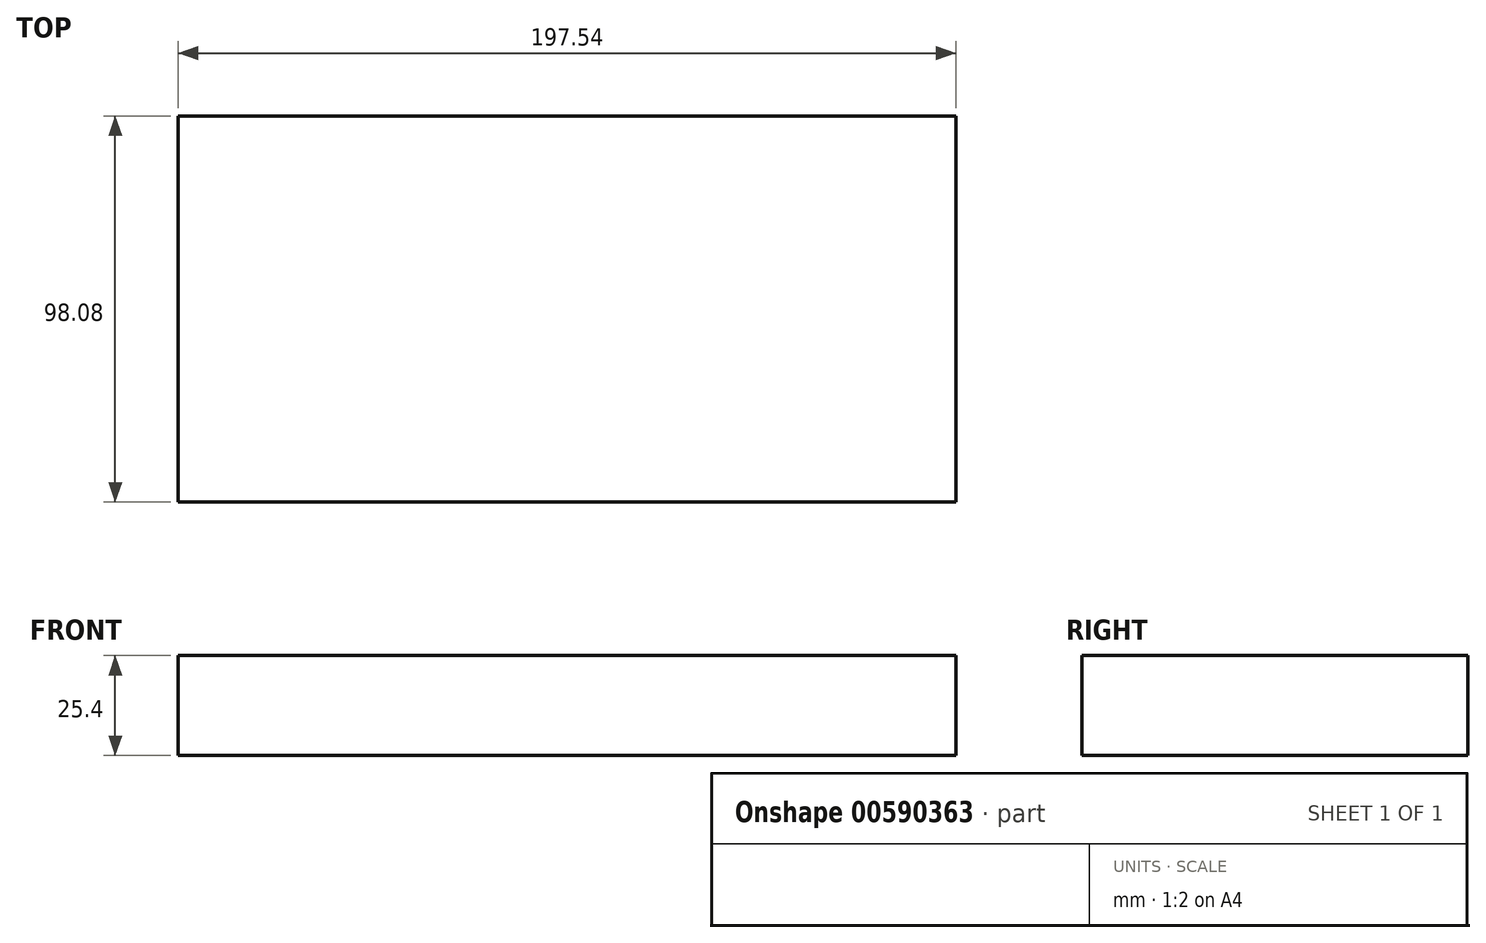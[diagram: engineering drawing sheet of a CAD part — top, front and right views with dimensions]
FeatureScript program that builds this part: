
annotation { "Feature Type Name" : "Feature", "Feature Type Description" : "" }
export const myFeature = defineFeature(function(context is Context, id is Id, definition is map)
    precondition{}
    {
        {
            var Q0;
            Q0=qCreatedBy(makeId("Top.planeOp"),FACE);
            var sketch = newSketch(context, id + "F0", { "sketchPlane" : qUnion([Q0])});
            skLineSegment(sketch, "E0.bottom", {"start": v(-140.42, 17.62) * mm, "end": v(57.12, 17.62) * mm});
            skLineSegment(sketch, "E0.top", {"start": v(-140.42, -80.46) * mm, "end": v(57.12, -80.46) * mm});
            skLineSegment(sketch, "E0.left", {"start": v(-140.42, 17.62) * mm, "end": v(-140.42, -80.46) * mm});
            skLineSegment(sketch, "E0.right", {"start": v(57.12, 17.62) * mm, "end": v(57.12, -80.46) * mm});
            skSolve(sketch);
        }
        {
            var Q0;
            Q0=makeQuery(id+"F0.imprint","IMPRINT",FACE,{"disambiguationData":[TD([[makeQuery(id+"F0.imprint","IMPRINT",EDGE,{"derivedFrom":sQuery(id+"F0.wireOp",EDGE,"E0.bottom")}),-1.0]])]});
            extrude(context, id + "F1", {"entities" : qUnion([Q0]), "depth" : 25.4 * mm, "offsetDistance" : 25.4 * mm});
        }
    });
